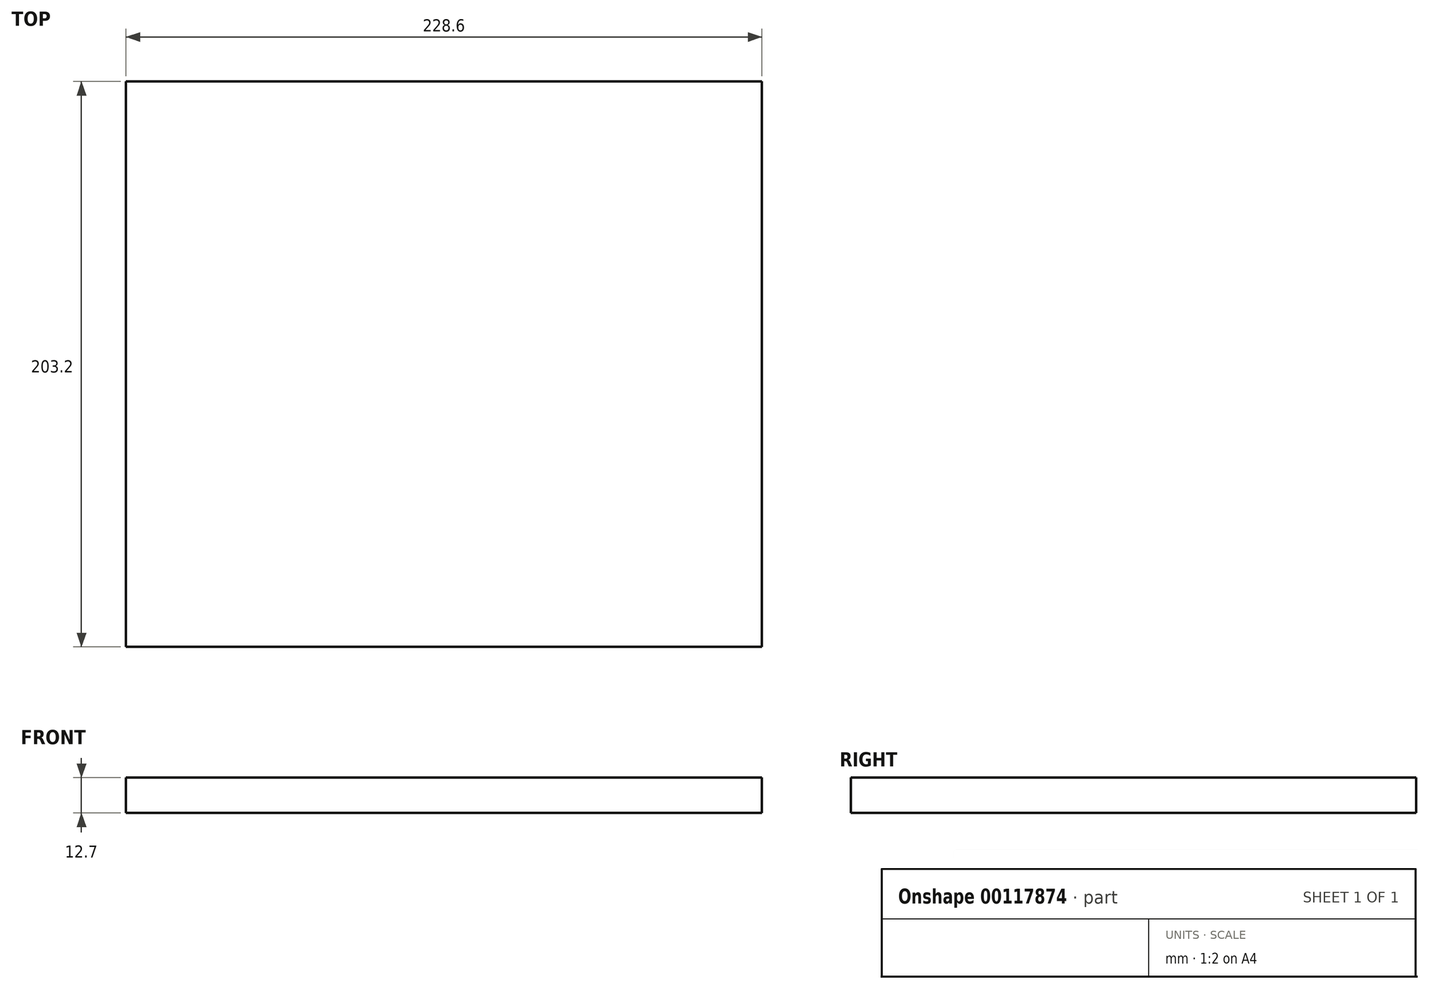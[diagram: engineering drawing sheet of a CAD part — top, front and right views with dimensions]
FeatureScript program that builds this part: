
annotation { "Feature Type Name" : "Feature", "Feature Type Description" : "" }
export const myFeature = defineFeature(function(context is Context, id is Id, definition is map)
    precondition{}
    {
        {
            var Q0;
            Q0=qCreatedBy(makeId("Top.planeOp"),FACE);
            var sketch = newSketch(context, id + "F0", { "sketchPlane" : qUnion([Q0])});
            skLineSegment(sketch, "E0.bottom", {"start": v(-114.3, -101.6) * mm, "end": v(114.3, -101.6) * mm});
            skLineSegment(sketch, "E0.top", {"start": v(-114.3, 101.6) * mm, "end": v(114.3, 101.6) * mm});
            skLineSegment(sketch, "E0.left", {"start": v(-114.3, -101.6) * mm, "end": v(-114.3, 101.6) * mm});
            skLineSegment(sketch, "E0.right", {"start": v(114.3, -101.6) * mm, "end": v(114.3, 101.6) * mm});
            skPoint(sketch, "E0.middle", {"position": v(0, 0) * mm});
            skSolve(sketch);
        }
        {
            var Q0;
            Q0 = qSketchRegion(id + "F0", true);
            extrude(context, id + "F1", {"entities" : qUnion([Q0]), "depth" : 12.7 * mm});
        }
    });
